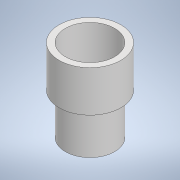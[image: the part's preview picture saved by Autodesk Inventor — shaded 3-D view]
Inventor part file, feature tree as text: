
AUTODESK INVENTOR PART (.ipt)
format: ipt  version: 2022.3 (Build 263350000, 350)  size: 103,424 bytes
history: native  units: mm
features: extrude x2, sketch x1
ambient origin geometry x8: Origin, YZ Plane, XZ Plane, XY Plane, X Axis, Y Axis, Z Axis, Center Point
bodies: Solid1 (feature_tree)
feature tree (3):
  sketch  "Sketch1"  dims[d0=24.0mm d1=30.0mm d2=20.0mm d3=0.0mm d4=20.0mm d5=0.0mm]
  extrude  "Extrusion1"  Depth=20.0mm
  extrude  "Extrusion2"  Depth=20.0mm TaperAngle=0.0deg
